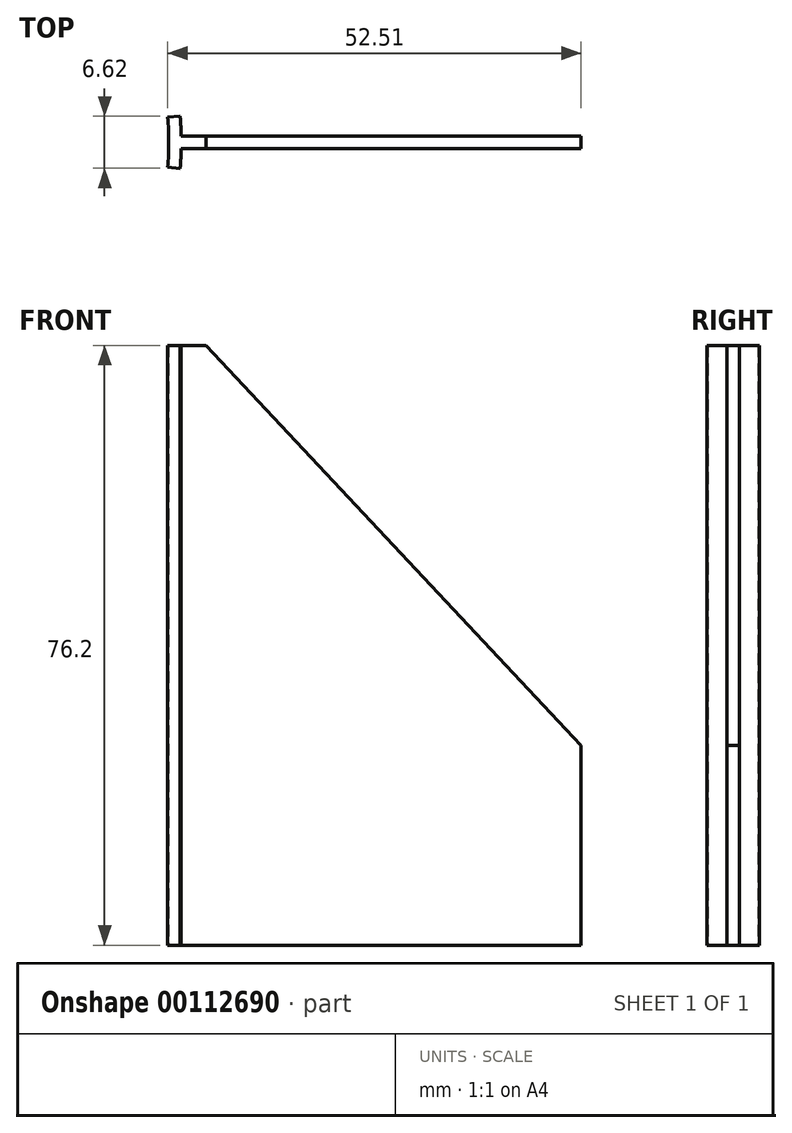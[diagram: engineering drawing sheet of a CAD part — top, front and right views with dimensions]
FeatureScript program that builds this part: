
annotation { "Feature Type Name" : "Feature", "Feature Type Description" : "" }
export const myFeature = defineFeature(function(context is Context, id is Id, definition is map)
    precondition{}
    {
        {
            var Q0;
            Q0=qCreatedBy(makeId("Top.planeOp"),FACE);
            var sketch = newSketch(context, id + "F0", { "sketchPlane" : qUnion([Q0])});
            skLineSegment(sketch, "E0.bottom", {"start": v(0, 0) * mm, "end": v(50.8, 0) * mm});
            skLineSegment(sketch, "E0.top", {"start": v(0, -1.59) * mm, "end": v(50.8, -1.59) * mm});
            skLineSegment(sketch, "E0.left", {"start": v(0, 0) * mm, "end": v(0, -1.59) * mm, "construction": true});
            skLineSegment(sketch, "E0.right", {"start": v(50.8, 0) * mm, "end": v(50.8, -1.59) * mm});
            skLineSegment(sketch, "E1", {"start": v(0, -0.8) * mm, "end": v(-1.58, -0.8) * mm, "construction": true});
            skArc(sketch, "E2", {"start": v(-1.71, -3.97) * mm, "mid": v(-1.58, -0.8) * mm, "end": v(-1.71, 2.38) * mm});
            skLineSegment(sketch, "E3", {"start": v(-1.58, -0.8) * mm, "end": v(-38.9, -0.8) * mm, "construction": true});
            skLineSegment(sketch, "E4", {"start": v(-38.9, -0.8) * mm, "end": v(-1.71, -3.97) * mm, "construction": true});
            skLineSegment(sketch, "E5", {"start": v(-38.9, -0.8) * mm, "end": v(-1.71, 2.38) * mm, "construction": true});
            skLineSegment(sketch, "E6", {"start": v(-1.71, 2.38) * mm, "end": v(-0.13, 2.52) * mm});
            skLineSegment(sketch, "E7", {"start": v(-1.71, -3.97) * mm, "end": v(-0.13, -4.1) * mm});
            skArc(sketch, "E8", {"start": v(-0.13, -4.1) * mm, "mid": v(-0.05, -2.85) * mm, "end": v(0, -1.59) * mm});
            skArc(sketch, "E9", {"start": v(0, 0) * mm, "mid": v(-0.05, 1.26) * mm, "end": v(-0.13, 2.52) * mm});
            skLineSegment(sketch, "E10", {"start": v(-1.71, -3.97) * mm, "end": v(-1.71, 2.38) * mm, "construction": true});
            skSolve(sketch);
        }
        {
            var Q0;
            Q0 = qSketchRegion(id + "F0", true);
            extrude(context, id + "F1", {"entities" : qUnion([Q0]), "depth" : 76.2 * mm});
        }
        {
            var Q0;
            Q0=makeQuery(id+"F1.opExtrude","SWEPT_FACE",FACE,{"disambiguationData":[OSD([sQuery(id+"F0.wireOp",EDGE,"E0.top")])]});
            var sketch = newSketch(context, id + "F2", { "sketchPlane" : qUnion([Q0])});
            skLineSegment(sketch, "E11", {"start": v(0, 76.2) * mm, "end": v(3.18, 76.2) * mm, "construction": true});
            skLineSegment(sketch, "E12", {"start": v(50.8, 0) * mm, "end": v(50.8, 25.4) * mm, "construction": true});
            skLineSegment(sketch, "E13", {"start": v(3.17, 76.2) * mm, "end": v(50.8, 25.4) * mm});
            skLineSegment(sketch, "E14.bottom", {"start": v(3.18, 76.2) * mm, "end": v(50.8, 76.2) * mm});
            skLineSegment(sketch, "E14.right", {"start": v(50.8, 76.2) * mm, "end": v(50.8, 25.4) * mm});
            skSolve(sketch);
        }
        {
            var Q0;
            Q0 = qSketchRegion(id + "F2", true);
            var Q1;
            Q1=makeQuery(id+"F1.opExtrude","SWEPT_FACE",FACE,{"disambiguationData":[OSD([sQuery(id+"F0.wireOp",EDGE,"E0.bottom")])]});
            extrude(context, id + "F3", {"entities" : qUnion([Q0]), "operationType" : NewBodyOperationType.REMOVE, "endBound" : BoundingType.UP_TO_SURFACE, "oppositeDirection" : true, "endBoundEntityFace" : qUnion([Q1]), "depth" : 25.4 * mm});
        }
    });
